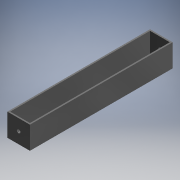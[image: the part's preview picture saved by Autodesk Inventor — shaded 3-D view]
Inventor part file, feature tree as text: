
AUTODESK INVENTOR PART (.ipt)
format: ipt  version: 2019 (Build 230136000, 136)  size: 110,592 bytes
history: native  units: mm (DEFAULTED — no unit token found)
features: extrude x3, sketch x3
ambient origin geometry x8: Origin, YZ Plane, XZ Plane, XY Plane, X Axis, Y Axis, Z Axis, Center Point
bodies: Solid1 (feature_tree)
feature tree (6):
  extrude  "Extrusion1"  Depth=31.75mm
  extrude  "Extrusion2"  Depth=200.406mm
  extrude  "Extrusion3"  Depth=29.718mm
  sketch  "Sketch1"  dims[d0=31.75mm d1=31.75mm]
  sketch  "Sketch2"  dims[d2=200.406mm d3=0.0mm d4=5.08mm]
  sketch  "Sketch3"  dims[d5=31.75mm d6=15.875mm d7=15.875mm d8=269.24mm d9=0.0mm d10=2.032mm d11=2.032mm d12=2.032mm d13=2.032mm d14=29.718mm d15=0.0mm]
